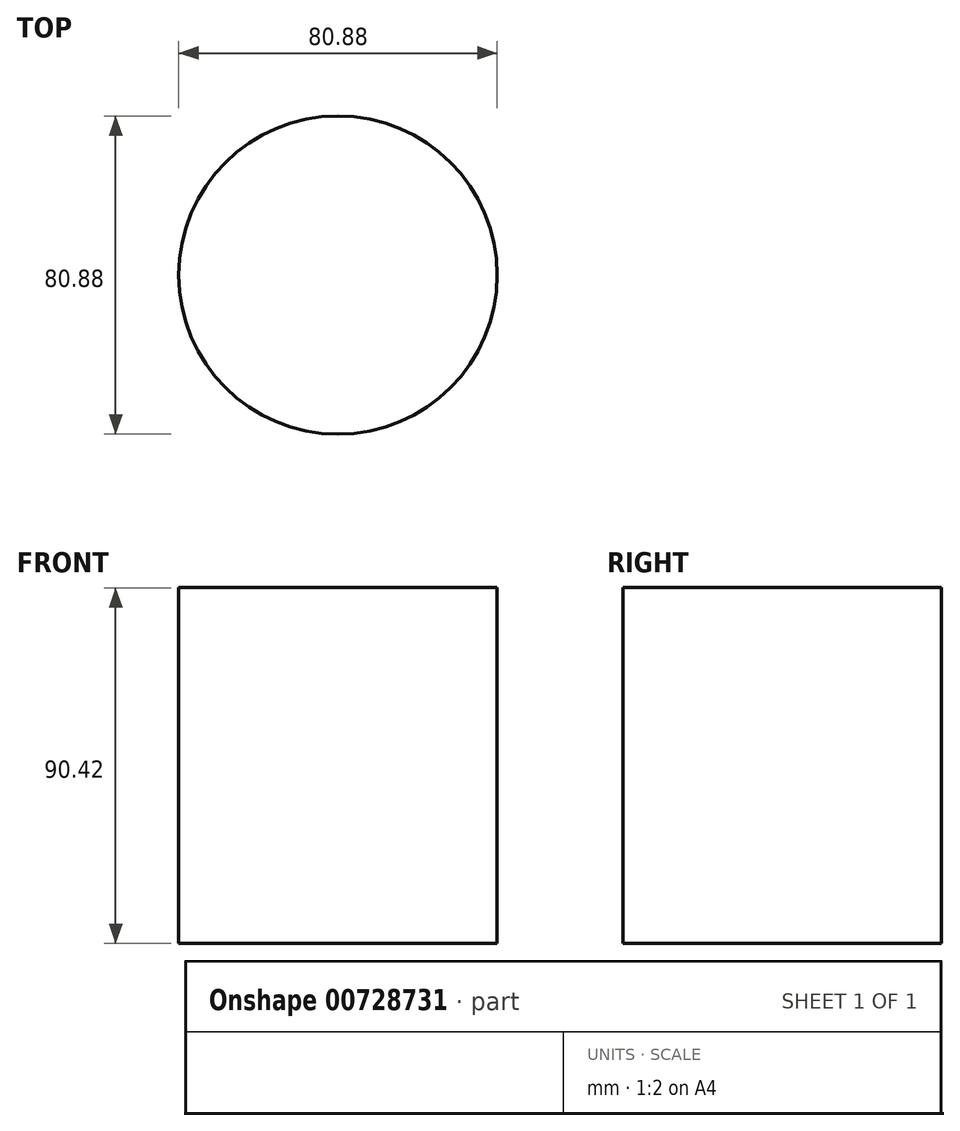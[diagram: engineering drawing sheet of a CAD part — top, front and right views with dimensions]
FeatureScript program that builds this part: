
annotation { "Feature Type Name" : "Feature", "Feature Type Description" : "" }
export const myFeature = defineFeature(function(context is Context, id is Id, definition is map)
    precondition{}
    {
        {
            var Q0;
            Q0=qCreatedBy(makeId("Top.planeOp"),FACE);
            var sketch = newSketch(context, id + "F0", { "sketchPlane" : qUnion([Q0])});
            skCircle(sketch, "E0", {"center": v(0, 0) * mm, "radius": 40.44 * mm});
            skSolve(sketch);
        }
        {
            var Q0;
            Q0=makeQuery(id+"F0.imprint","IMPRINT",FACE,{"disambiguationData":[TD([[makeQuery(id+"F0.imprint","IMPRINT",EDGE,{"derivedFrom":sQuery(id+"F0.wireOp",EDGE,"E0")}),1.0]])]});
            extrude(context, id + "F1", {"entities" : qUnion([Q0]), "depth" : 90.42 * mm, "offsetDistance" : 25.4 * mm});
        }
    });
